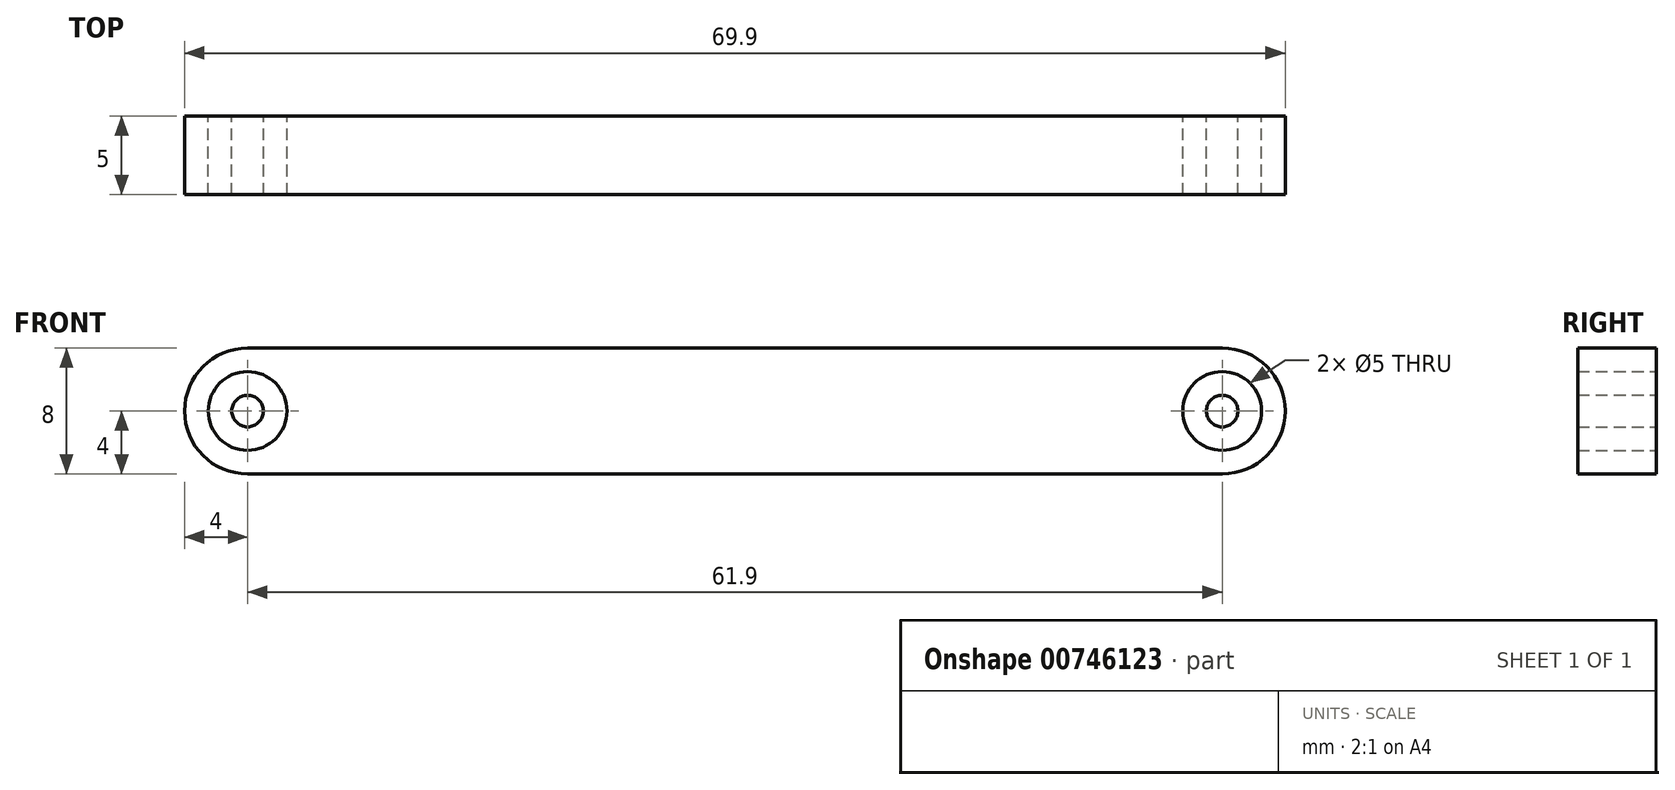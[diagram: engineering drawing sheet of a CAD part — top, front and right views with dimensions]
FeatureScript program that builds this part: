
annotation { "Feature Type Name" : "Feature", "Feature Type Description" : "" }
export const myFeature = defineFeature(function(context is Context, id is Id, definition is map)
    precondition{}
    {
        {
            var Q0;
            Q0=qCreatedBy(makeId("Front.planeOp"),FACE);
            var sketch = newSketch(context, id + "F0", { "sketchPlane" : qUnion([Q0])});
            skCircle(sketch, "E0", {"center": v(0, 0) * mm, "radius": 2.5 * mm});
            skArc(sketch, "E1", {"start": v(0, 4) * mm, "mid": v(-4, 0) * mm, "end": v(0, -4) * mm});
            skCircle(sketch, "E2", {"center": v(0, 0) * mm, "radius": 1 * mm});
            skArc(sketch, "E3", {"start": v(61.9, -4) * mm, "mid": v(65.9, 0) * mm, "end": v(61.9, 4) * mm});
            skCircle(sketch, "E4", {"center": v(61.9, 0) * mm, "radius": 2.5 * mm});
            skCircle(sketch, "E5", {"center": v(61.9, 0) * mm, "radius": 1 * mm});
            skLineSegment(sketch, "E6", {"start": v(0, 4) * mm, "end": v(61.9, 4) * mm});
            skLineSegment(sketch, "E7.0", {"start": v(0, -4) * mm, "end": v(61.9, -4) * mm});
            skSolve(sketch);
        }
        {
            var Q0;
            Q0=makeQuery(id+"F0.imprint","IMPRINT",FACE,{"disambiguationData":[TD([[makeQuery(id+"F0.imprint","IMPRINT",EDGE,{"derivedFrom":sQuery(id+"F0.wireOp",EDGE,"E0")}),-1.0]])]});
            var Q1;
            Q1=makeQuery(id+"F0.imprint","IMPRINT",FACE,{"disambiguationData":[TD([[makeQuery(id+"F0.imprint","IMPRINT",EDGE,{"derivedFrom":sQuery(id+"F0.wireOp",EDGE,"E5")}),1.0]])]});
            var Q2;
            Q2=makeQuery(id+"F0.imprint","IMPRINT",FACE,{"disambiguationData":[TD([[makeQuery(id+"F0.imprint","IMPRINT",EDGE,{"derivedFrom":sQuery(id+"F0.wireOp",EDGE,"E2")}),1.0]])]});
            extrude(context, id + "F1", {"entities" : qUnion([Q0, Q1, Q2]), "depth" : 5 * mm, "offsetDistance" : 25.4 * mm});
        }
    });
